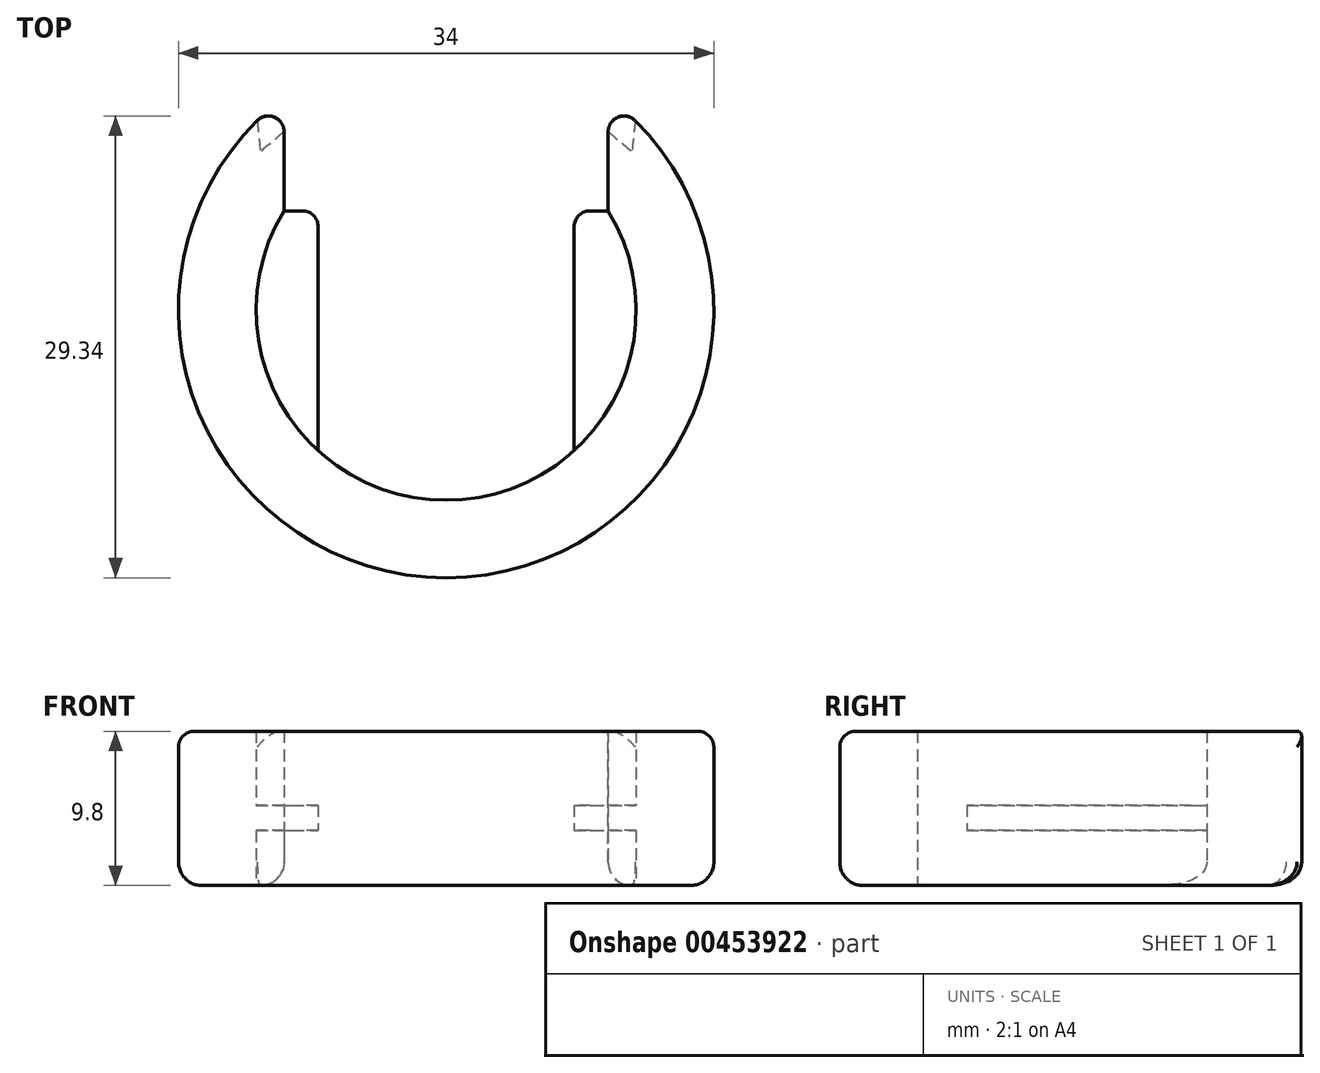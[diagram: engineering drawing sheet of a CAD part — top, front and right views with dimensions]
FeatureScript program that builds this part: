
annotation { "Feature Type Name" : "Feature", "Feature Type Description" : "" }
export const myFeature = defineFeature(function(context is Context, id is Id, definition is map)
    precondition{}
    {
        {
            var Q0;
            Q0=qCreatedBy(makeId("Top.planeOp"),FACE);
            var sketch = newSketch(context, id + "F0", { "sketchPlane" : qUnion([Q0])});
            skCircle(sketch, "E0", {"center": v(0, 0) * mm, "radius": 8.13 * mm});
            skCircle(sketch, "E1", {"center": v(0, 0) * mm, "radius": 12.07 * mm});
            skCircle(sketch, "E2", {"center": v(0, 0) * mm, "radius": 17 * mm});
            skLineSegment(sketch, "E3", {"start": v(-8.13, 0) * mm, "end": v(-8.13, 8.92) * mm});
            skLineSegment(sketch, "E4", {"start": v(-8.13, 0) * mm, "end": v(-8.13, -8.92) * mm});
            skLineSegment(sketch, "E5", {"start": v(8.13, 0) * mm, "end": v(8.13, 8.92) * mm});
            skLineSegment(sketch, "E6", {"start": v(8.13, 0) * mm, "end": v(8.13, -8.92) * mm});
            skLineSegment(sketch, "E7", {"start": v(-10.3, 6.3) * mm, "end": v(10.3, 6.3) * mm});
            skLineSegment(sketch, "E8", {"start": v(-10.3, 6.3) * mm, "end": v(-10.3, 13.53) * mm});
            skLineSegment(sketch, "E9", {"start": v(10.3, 6.3) * mm, "end": v(10.3, 13.53) * mm});
            skSolve(sketch);
        }
        {
            var Q0;
            {var subQ0=sQuery(id+"F0.wireOp",EDGE,"E8");Q0=makeQuery(id+"F0.imprint","IMPRINT",FACE,{"disambiguationData":[TD([[makeQuery(id+"F0.imprint","IMPRINT",EDGE,{"derivedFrom":subQ0}),1.0]])]});}
            extrude(context, id + "F1", {"entities" : qUnion([Q0]), "depth" : 9.8 * mm});
        }
        {
            var Q0;
            {var subQ0=sQuery(id+"F0.wireOp",EDGE,"E4");Q0=makeQuery(id+"F0.imprint","IMPRINT",FACE,{"disambiguationData":[TD([[makeQuery(id+"F0.imprint","IMPRINT",EDGE,{"derivedFrom":subQ0}),-1.0]])]});}
            var Q1;
            {var subQ0=sQuery(id+"F0.wireOp",EDGE,"E6");Q1=makeQuery(id+"F0.imprint","IMPRINT",FACE,{"disambiguationData":[TD([[makeQuery(id+"F0.imprint","IMPRINT",EDGE,{"derivedFrom":subQ0}),1.0]])]});}
            extrude(context, id + "F2", {"entities" : qUnion([Q0, Q1]), "operationType" : NewBodyOperationType.ADD, "depth" : 5.1 * mm});
        }
        {
            var Q0;
            {var subQ0=sQuery(id+"F0.wireOp",EDGE,"E6");Q0=makeQuery(id+"F0.imprint","IMPRINT",FACE,{"disambiguationData":[TD([[makeQuery(id+"F0.imprint","IMPRINT",EDGE,{"derivedFrom":subQ0}),1.0]])]});}
            var Q1;
            {var subQ0=sQuery(id+"F0.wireOp",EDGE,"E4");Q1=makeQuery(id+"F0.imprint","IMPRINT",FACE,{"disambiguationData":[TD([[makeQuery(id+"F0.imprint","IMPRINT",EDGE,{"derivedFrom":subQ0}),-1.0]])]});}
            extrude(context, id + "F3", {"entities" : qUnion([Q0, Q1]), "operationType" : NewBodyOperationType.REMOVE, "depth" : 3.5 * mm});
        }
        {
            var Q0;
            Q0=makeQuery(id+"F1.opExtrude","CAP_EDGE",EDGE,{"disambiguationData":[OSD([sQuery(id+"F0.wireOp",EDGE,"E2")])],"isStart":false});
            var Q1;
            Q1=makeQuery(id+"F1.opExtrude","SWEPT_EDGE",EDGE,{"disambiguationData":[OSD([sQuery(id+"F0.wireOp",EDGE,"E2"),sQuery(id+"F0.wireOp",EDGE,"E8")])]});
            var Q2;
            Q2=makeQuery(id+"F1.opExtrude","SWEPT_EDGE",EDGE,{"disambiguationData":[OSD([sQuery(id+"F0.wireOp",EDGE,"E2"),sQuery(id+"F0.wireOp",EDGE,"E9")])]});
            var Q3;
            Q3=makeQuery(id+"F2.opExtrude","SWEPT_EDGE",EDGE,{"disambiguationData":[OSD([sQuery(id+"F0.wireOp",EDGE,"E3"),sQuery(id+"F0.wireOp",EDGE,"E7")])]});
            var Q4;
            Q4=makeQuery(id+"F2.opExtrude","SWEPT_EDGE",EDGE,{"disambiguationData":[OSD([sQuery(id+"F0.wireOp",EDGE,"E5"),sQuery(id+"F0.wireOp",EDGE,"E7")])]});
            fillet(context, id + "F4", {"entities" : qUnion([Q0, Q1, Q2, Q3, Q4]), "radius" : 1 * mm, "tangentPropagation" : true, "allowEdgeOverflow" : false});
        }
        {
            var Q0;
            Q0=makeQuery(id+"F1.opExtrude","CAP_EDGE",EDGE,{"disambiguationData":[OSD([sQuery(id+"F0.wireOp",EDGE,"E2")])],"isStart":true});
            var Q1;
            {var subQ0=sQuery(id+"F0.wireOp",EDGE,"E1");Q1=makeQuery(id+"F3.boolean.opBoolean","MERGE",EDGE,{"derivedFrom":[makeQuery(id+"F1.opExtrude","CAP_EDGE",EDGE,{"disambiguationData":[OSD([subQ0])],"isStart":true}),makeQuery(id+"F3.opExtrude","CAP_EDGE",EDGE,{"disambiguationData":[OSD([subQ0]),TDD([makeQuery(id+"F0.imprint","IMPRINT",EDGE,{"disambiguationData":[TD([[makeQuery(id+"F0.imprint","INTERSECT",VERTEX,{"derivedFrom":[subQ0,sQuery(id+"F0.wireOp",EDGE,"E4")]}),1.0]])],"derivedFrom":subQ0})])],"isStart":true}),makeQuery(id+"F3.opExtrude","CAP_EDGE",EDGE,{"disambiguationData":[OSD([subQ0]),TDD([makeQuery(id+"F0.imprint","IMPRINT",EDGE,{"disambiguationData":[TD([[makeQuery(id+"F0.imprint","INTERSECT",VERTEX,{"derivedFrom":[subQ0,sQuery(id+"F0.wireOp",EDGE,"E6")]}),-1.0]])],"derivedFrom":subQ0})])],"isStart":true})]});}
            fillet(context, id + "F5", {"entities" : qUnion([Q0, Q1]), "radius" : 1.5 * mm, "tangentPropagation" : true, "allowEdgeOverflow" : false});
        }
    });
